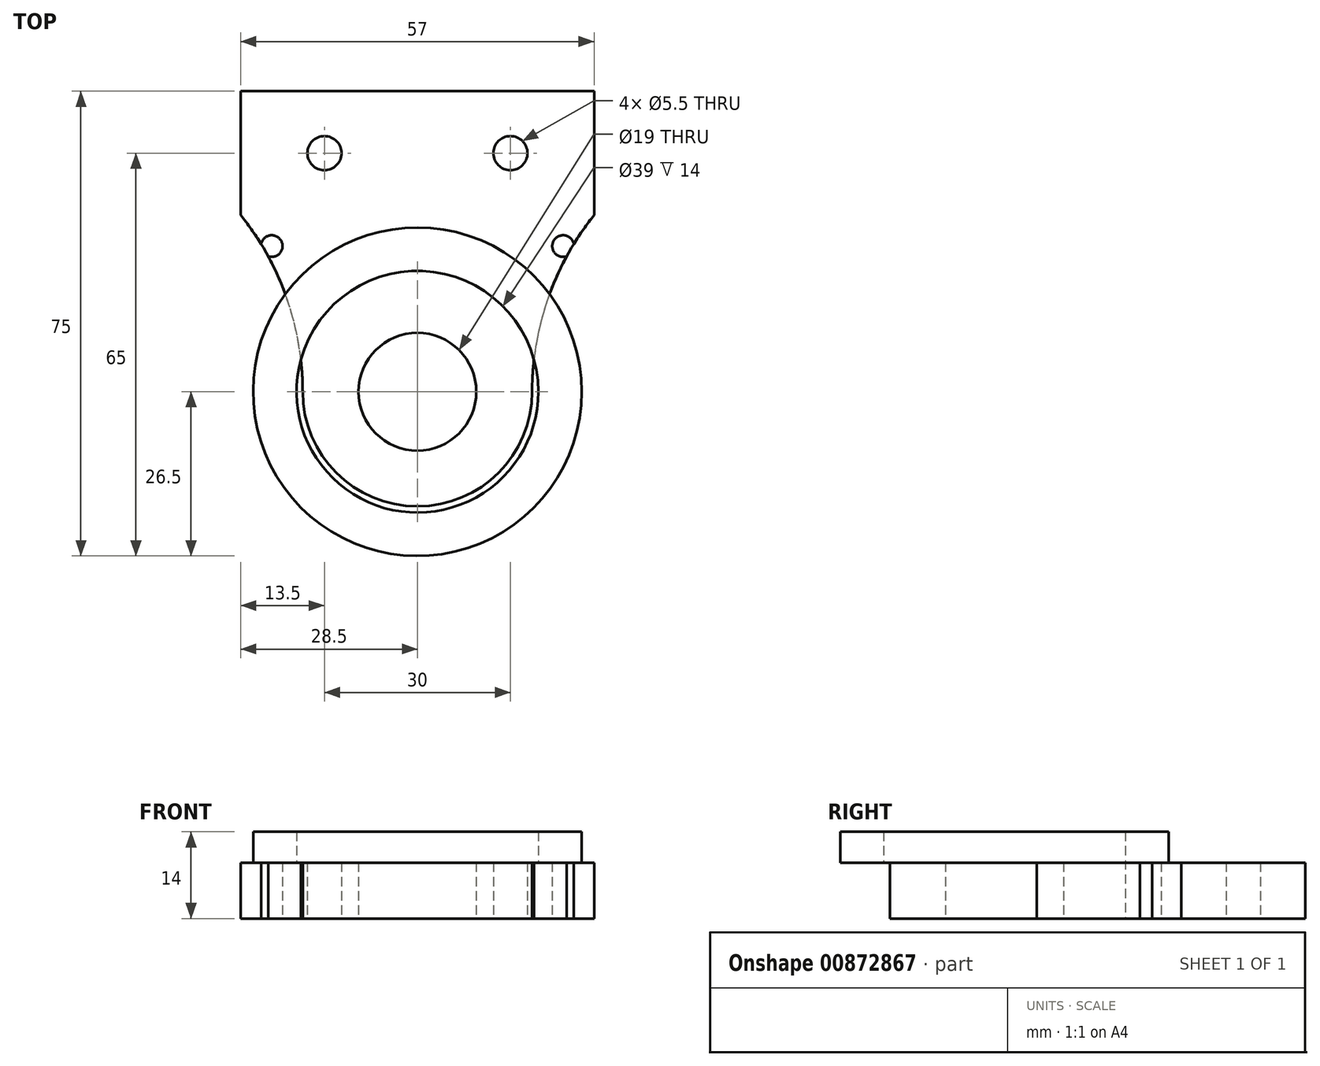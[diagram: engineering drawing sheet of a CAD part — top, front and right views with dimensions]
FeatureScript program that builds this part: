
annotation { "Feature Type Name" : "Feature", "Feature Type Description" : "" }
export const myFeature = defineFeature(function(context is Context, id is Id, definition is map)
    precondition{}
    {
        {
            var Q0;
            Q0=qCreatedBy(makeId("Top.planeOp"),FACE);
            var sketch = newSketch(context, id + "F0", { "sketchPlane" : qUnion([Q0])});
            skCircle(sketch, "E0", {"center": v(0, 0) * mm, "radius": 19.5 * mm});
            skLineSegment(sketch, "E1.bottom", {"start": v(-23.5, 23.5) * mm, "end": v(23.5, 23.5) * mm, "construction": true});
            skLineSegment(sketch, "E1.top", {"start": v(-23.5, -23.5) * mm, "end": v(23.5, -23.5) * mm, "construction": true});
            skLineSegment(sketch, "E1.left", {"start": v(-23.5, 23.5) * mm, "end": v(-23.5, -23.5) * mm, "construction": true});
            skLineSegment(sketch, "E1.right", {"start": v(23.5, 23.5) * mm, "end": v(23.5, -23.5) * mm, "construction": true});
            skCircle(sketch, "E2", {"center": v(-23.5, 23.5) * mm, "radius": 1.75 * mm});
            skCircle(sketch, "E3", {"center": v(23.5, 23.5) * mm, "radius": 1.75 * mm});
            skCircle(sketch, "E4", {"center": v(23.5, -23.5) * mm, "radius": 1.75 * mm});
            skCircle(sketch, "E5", {"center": v(-23.5, -23.5) * mm, "radius": 1.75 * mm});
            skLineSegment(sketch, "E6.bottom", {"start": v(-28.5, 28.5) * mm, "end": v(28.5, 28.5) * mm});
            skLineSegment(sketch, "E6.top", {"start": v(-28.5, -28.5) * mm, "end": v(28.5, -28.5) * mm});
            skLineSegment(sketch, "E6.left", {"start": v(-28.5, 28.5) * mm, "end": v(-28.5, -28.5) * mm});
            skLineSegment(sketch, "E6.right", {"start": v(28.5, 28.5) * mm, "end": v(28.5, -28.5) * mm});
            skLineSegment(sketch, "E7", {"start": v(-28.5, 28.5) * mm, "end": v(-28.5, 48.5) * mm});
            skLineSegment(sketch, "E8", {"start": v(28.5, 48.5) * mm, "end": v(-28.5, 48.5) * mm});
            skLineSegment(sketch, "E9", {"start": v(28.5, 48.5) * mm, "end": v(28.5, 28.5) * mm});
            skLineSegment(sketch, "E10", {"start": v(-28.5, 38.5) * mm, "end": v(28.5, 38.5) * mm, "construction": true});
            skCircle(sketch, "E11", {"center": v(-15, 38.5) * mm, "radius": 2.75 * mm});
            skCircle(sketch, "E12", {"center": v(15, 38.5) * mm, "radius": 2.75 * mm});
            skCircle(sketch, "E13", {"center": v(0, 0) * mm, "radius": 9.5 * mm});
            skSolve(sketch);
        }
        {
            var Q0;
            Q0=makeQuery(id+"F0.imprint","IMPRINT",FACE,{"disambiguationData":[TD([[makeQuery(id+"F0.imprint","IMPRINT",EDGE,{"derivedFrom":sQuery(id+"F0.wireOp",EDGE,"E6.bottom")}),1.0]])]});
            var Q1;
            Q1=makeQuery(id+"F0.imprint","IMPRINT",FACE,{"disambiguationData":[TD([[makeQuery(id+"F0.imprint","IMPRINT",EDGE,{"derivedFrom":sQuery(id+"F0.wireOp",EDGE,"E0")}),-1.0]])]});
            extrude(context, id + "F1", {"entities" : qUnion([Q0, Q1]), "depth" : 9 * mm, "offsetDistance" : 25 * mm});
        }
        {
            var Q0;
            Q0=makeQuery(id+"F1.opExtrude","CAP_FACE",FACE,{"disambiguationData":[OSD([sQuery(id+"F0.wireOp",EDGE,"E0"),sQuery(id+"F0.wireOp",EDGE,"E2"),sQuery(id+"F0.wireOp",EDGE,"E3"),sQuery(id+"F0.wireOp",EDGE,"E4"),sQuery(id+"F0.wireOp",EDGE,"E5"),sQuery(id+"F0.wireOp",EDGE,"E6.top"),sQuery(id+"F0.wireOp",EDGE,"E6.left"),sQuery(id+"F0.wireOp",EDGE,"E6.right"),sQuery(id+"F0.wireOp",EDGE,"E7"),sQuery(id+"F0.wireOp",EDGE,"E8"),sQuery(id+"F0.wireOp",EDGE,"E9"),sQuery(id+"F0.wireOp",EDGE,"E11"),sQuery(id+"F0.wireOp",EDGE,"E12")])],"isStart":false});
            var sketch = newSketch(context, id + "F2", { "sketchPlane" : qUnion([Q0])});
            skCircle(sketch, "E14", {"center": v(0, 0) * mm, "radius": 19.5 * mm});
            skCircle(sketch, "E15", {"center": v(0, 0) * mm, "radius": 26.5 * mm});
            skSolve(sketch);
        }
        {
            var Q0;
            Q0=makeQuery(id+"F2.imprint","IMPRINT",FACE,{"disambiguationData":[TD([[makeQuery(id+"F2.imprint","IMPRINT",EDGE,{"derivedFrom":sQuery(id+"F2.wireOp",EDGE,"E14")}),-1.0]])]});
            extrude(context, id + "F3", {"entities" : qUnion([Q0]), "operationType" : NewBodyOperationType.ADD, "depth" : 5 * mm, "offsetDistance" : 25 * mm});
        }
        {
            var Q0;
            Q0=makeQuery(id+"F0.imprint","IMPRINT",FACE,{"disambiguationData":[TD([[makeQuery(id+"F0.imprint","IMPRINT",EDGE,{"derivedFrom":sQuery(id+"F0.wireOp",EDGE,"E0")}),1.0]])]});
            var Q1;
            Q1=makeQuery(id+"F0.imprint","IMPRINT",FACE,{"disambiguationData":[TD([[makeQuery(id+"F0.imprint","IMPRINT",EDGE,{"derivedFrom":sQuery(id+"F0.wireOp",EDGE,"E0")}),-1.0]])]});
            var Q2;
            Q2=makeQuery(id+"F0.imprint","IMPRINT",FACE,{"disambiguationData":[TD([[makeQuery(id+"F0.imprint","IMPRINT",EDGE,{"derivedFrom":sQuery(id+"F0.wireOp",EDGE,"E3")}),1.0]])]});
            var Q3;
            Q3=makeQuery(id+"F0.imprint","IMPRINT",FACE,{"disambiguationData":[TD([[makeQuery(id+"F0.imprint","IMPRINT",EDGE,{"derivedFrom":sQuery(id+"F0.wireOp",EDGE,"E6.bottom")}),1.0]])]});
            var Q4;
            Q4=makeQuery(id+"F0.imprint","IMPRINT",FACE,{"disambiguationData":[TD([[makeQuery(id+"F0.imprint","IMPRINT",EDGE,{"derivedFrom":sQuery(id+"F0.wireOp",EDGE,"E5")}),1.0]])]});
            var Q5;
            Q5=makeQuery(id+"F0.imprint","IMPRINT",FACE,{"disambiguationData":[TD([[makeQuery(id+"F0.imprint","IMPRINT",EDGE,{"derivedFrom":sQuery(id+"F0.wireOp",EDGE,"E2")}),1.0]])]});
            var Q6;
            Q6=makeQuery(id+"F0.imprint","IMPRINT",FACE,{"disambiguationData":[TD([[makeQuery(id+"F0.imprint","IMPRINT",EDGE,{"derivedFrom":sQuery(id+"F0.wireOp",EDGE,"E4")}),1.0]])]});
            extrude(context, id + "F4", {"entities" : qUnion([Q0, Q1, Q2, Q3, Q4, Q5, Q6]), "depth" : 9 * mm, "offsetDistance" : 25 * mm});
        }
        {
            var Q0;
            Q0=makeQuery(id+"F4.opExtrude","CAP_FACE",FACE,{"disambiguationData":[OSD([sQuery(id+"F0.wireOp",EDGE,"E6.top"),sQuery(id+"F0.wireOp",EDGE,"E6.left"),sQuery(id+"F0.wireOp",EDGE,"E6.right"),sQuery(id+"F0.wireOp",EDGE,"E7"),sQuery(id+"F0.wireOp",EDGE,"E8"),sQuery(id+"F0.wireOp",EDGE,"E9"),sQuery(id+"F0.wireOp",EDGE,"E11"),sQuery(id+"F0.wireOp",EDGE,"E12"),sQuery(id+"F0.wireOp",EDGE,"E13")])],"isStart":false});
            var sketch = newSketch(context, id + "F5", { "sketchPlane" : qUnion([Q0])});
            skLineSegment(sketch, "E16", {"start": v(-28.5, 28.5) * mm, "end": v(28.5, 28.5) * mm, "construction": true});
            skLineSegment(sketch, "E17", {"start": v(-28.5, 0) * mm, "end": v(28.5, 0) * mm, "construction": true});
            skLineSegment(sketch, "E18", {"start": v(-18.5, 0) * mm, "end": v(-18.5, 28.5) * mm, "construction": true});
            skLineSegment(sketch, "E19", {"start": v(18.5, 0) * mm, "end": v(18.5, 28.5) * mm, "construction": true});
            skArc(sketch, "E20", {"start": v(-18.5, 0) * mm, "mid": v(0, -18.5) * mm, "end": v(18.5, 0) * mm});
            skArc(sketch, "E21", {"start": v(-18.5, 0) * mm, "mid": v(-21.07, 15.1) * mm, "end": v(-28.5, 28.5) * mm});
            skArc(sketch, "E22", {"start": v(28.5, 28.5) * mm, "mid": v(21.07, 15.1) * mm, "end": v(18.5, 0) * mm});
            skSolve(sketch);
        }
        {
            var Q0;
            Q0=makeQuery(id+"F5.imprint","IMPRINT",FACE,{"disambiguationData":[TD([[makeQuery(id+"F5.imprint","IMPRINT",EDGE,{"derivedFrom":sQuery(id+"F5.wireOp",EDGE,"E20")}),-1.0]])]});
            extrude(context, id + "F6", {"entities" : qUnion([Q0]), "operationType" : NewBodyOperationType.REMOVE, "endBound" : BoundingType.THROUGH_ALL, "oppositeDirection" : true, "depth" : 25 * mm, "offsetDistance" : 25 * mm});
        }
    });
